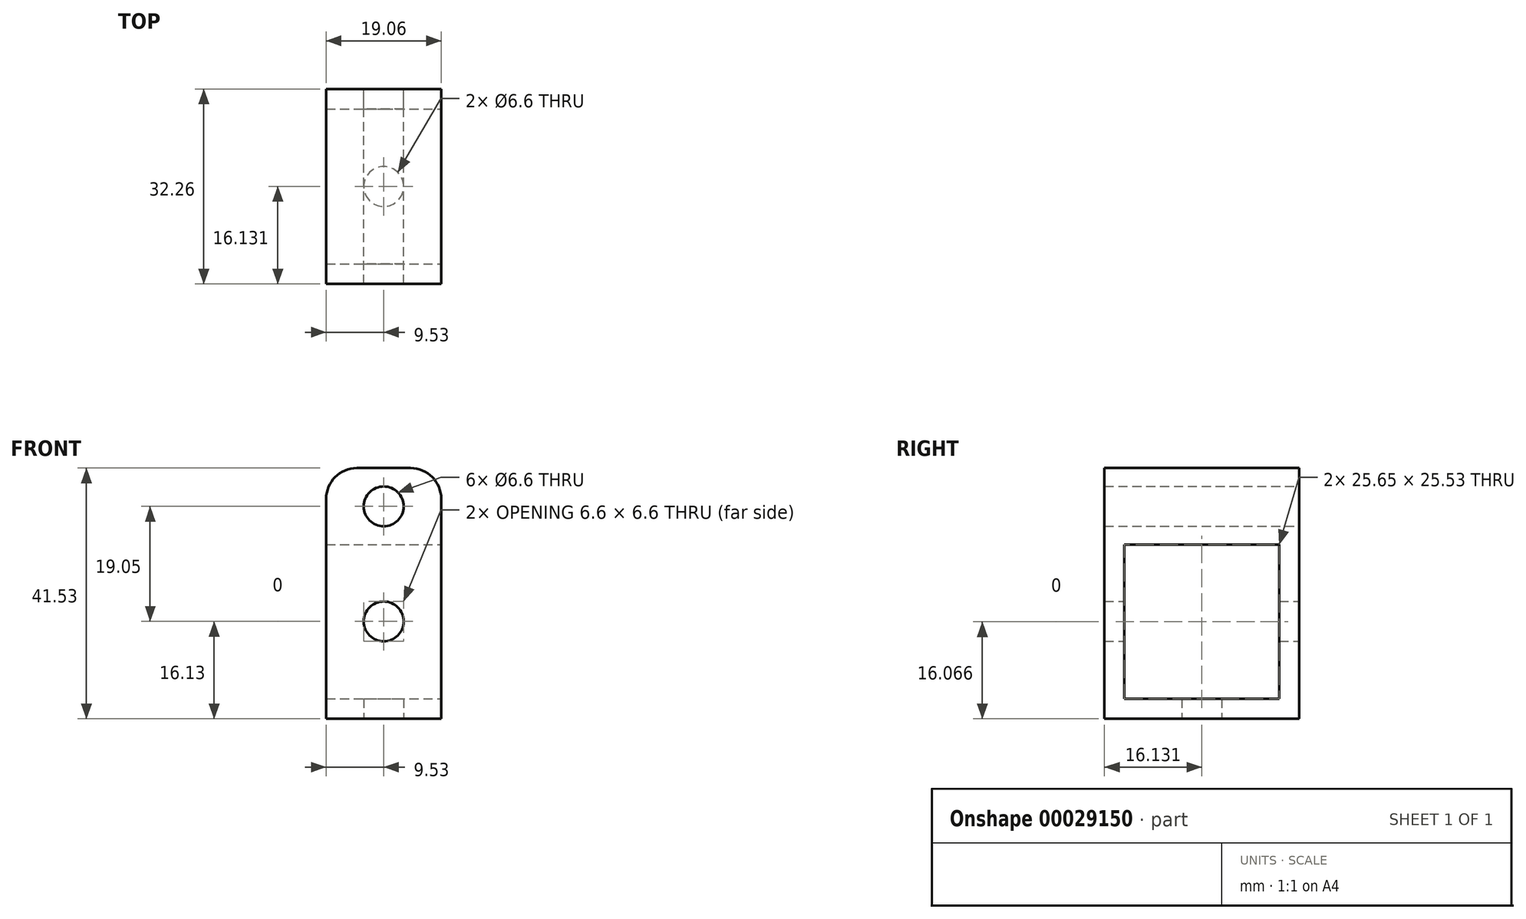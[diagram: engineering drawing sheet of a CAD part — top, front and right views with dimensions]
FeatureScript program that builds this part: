
annotation { "Feature Type Name" : "Feature", "Feature Type Description" : "" }
export const myFeature = defineFeature(function(context is Context, id is Id, definition is map)
    precondition{}
    {
        {
            var Q0;
            Q0=qCreatedBy(makeId("Front.planeOp"),FACE);
            var sketch = newSketch(context, id + "F0", { "sketchPlane" : qUnion([Q0])});
            skLineSegment(sketch, "E0", {"start": v(-9.53, 0) * mm, "end": v(0, 0) * mm, "construction": true});
            skLineSegment(sketch, "E1", {"start": v(-9.53, 0) * mm, "end": v(-9.53, 12.7) * mm});
            skLineSegment(sketch, "E2", {"start": v(-9.53, 12.7) * mm, "end": v(0, 12.7) * mm});
            skLineSegment(sketch, "E3", {"start": v(-9.53, 0) * mm, "end": v(-9.53, -28.83) * mm});
            skLineSegment(sketch, "E4", {"start": v(-9.53, -28.83) * mm, "end": v(0, -28.83) * mm});
            skLineSegment(sketch, "E5.MirrorCS", {"start": v(9.53, 12.7) * mm, "end": v(0, 12.7) * mm});
            skLineSegment(sketch, "E6.MirrorCS", {"start": v(9.53, 0) * mm, "end": v(9.53, 12.7) * mm});
            skLineSegment(sketch, "E7.MirrorCS", {"start": v(9.53, 0) * mm, "end": v(9.53, -28.83) * mm});
            skLineSegment(sketch, "E8.MirrorCS", {"start": v(9.53, -28.83) * mm, "end": v(0, -28.83) * mm});
            skLineSegment(sketch, "E9", {"start": v(0, 12.7) * mm, "end": v(0, 0) * mm, "construction": true});
            skCircle(sketch, "E10", {"center": v(0, 6.35) * mm, "radius": 3.3 * mm});
            skLineSegment(sketch, "E11", {"start": v(0, 0) * mm, "end": v(0, -25.4) * mm, "construction": true});
            skLineSegment(sketch, "E12", {"start": v(0, -25.4) * mm, "end": v(0, -28.83) * mm, "construction": true});
            skCircle(sketch, "E13", {"center": v(0, -12.7) * mm, "radius": 3.3 * mm});
            skSolve(sketch);
        }
        {
            var Q0;
            Q0=makeQuery(id+"F0.imprint","IMPRINT",FACE,{"disambiguationData":[TD([[makeQuery(id+"F0.imprint","IMPRINT",EDGE,{"derivedFrom":sQuery(id+"F0.wireOp",EDGE,"E1")}),-1.0]])]});
            extrude(context, id + "F1", {"entities" : qUnion([Q0]), "depth" : 32.26 * mm});
        }
        {
            var Q0;
            Q0=makeQuery(id+"F1.opExtrude","SWEPT_FACE",FACE,{"disambiguationData":[OSD([sQuery(id+"F0.wireOp",EDGE,"E6.MirrorCS"),sQuery(id+"F0.wireOp",EDGE,"E7.MirrorCS")])]});
            var sketch = newSketch(context, id + "F2", { "sketchPlane" : qUnion([Q0])});
            skLineSegment(sketch, "E14", {"start": v(-32.26, -25.53) * mm, "end": v(-28.96, -25.53) * mm, "construction": true});
            skLineSegment(sketch, "E15", {"start": v(-28.96, -25.53) * mm, "end": v(-3.3, -25.53) * mm, "construction": true});
            skLineSegment(sketch, "E16", {"start": v(-3.3, -25.53) * mm, "end": v(0, -25.53) * mm, "construction": true});
            skLineSegment(sketch, "E17", {"start": v(-16.13, -28.83) * mm, "end": v(-16.13, -25.53) * mm, "construction": true});
            skLineSegment(sketch, "E18", {"start": v(-28.96, -25.53) * mm, "end": v(-28.96, 0) * mm});
            skLineSegment(sketch, "E19", {"start": v(-28.96, -25.53) * mm, "end": v(-3.3, -25.53) * mm});
            skLineSegment(sketch, "E20", {"start": v(-3.3, -25.53) * mm, "end": v(-3.3, 0) * mm});
            skLineSegment(sketch, "E21", {"start": v(-3.3, 0) * mm, "end": v(-28.96, 0) * mm});
            skSolve(sketch);
        }
        {
            var Q0;
            Q0 = qSketchRegion(id + "F2", true);
            extrude(context, id + "F3", {"entities" : qUnion([Q0]), "operationType" : NewBodyOperationType.REMOVE, "oppositeDirection" : true, "depth" : 25.4 * mm});
        }
        {
            var Q0;
            Q0=makeQuery(id+"F1.opExtrude","SWEPT_FACE",FACE,{"disambiguationData":[OSD([sQuery(id+"F0.wireOp",EDGE,"E4"),sQuery(id+"F0.wireOp",EDGE,"E8.MirrorCS")])]});
            var sketch = newSketch(context, id + "F4", { "sketchPlane" : qUnion([Q0])});
            skLineSegment(sketch, "E22", {"start": v(0, 32.26) * mm, "end": v(0, 0) * mm, "construction": true});
            skCircle(sketch, "E23", {"center": v(0, 16.13) * mm, "radius": 3.3 * mm});
            skSolve(sketch);
        }
        {
            var Q0;
            Q0=makeQuery(id+"F4.imprint","IMPRINT",FACE,{"disambiguationData":[TD([[makeQuery(id+"F4.imprint","IMPRINT",EDGE,{"derivedFrom":sQuery(id+"F4.wireOp",EDGE,"E23")}),1.0]])]});
            extrude(context, id + "F5", {"entities" : qUnion([Q0]), "operationType" : NewBodyOperationType.REMOVE, "oppositeDirection" : true, "depth" : 12.7 * mm});
        }
        {
            var Q0;
            Q0=makeQuery(id+"F1.opExtrude","SWEPT_EDGE",EDGE,{"disambiguationData":[OSD([sQuery(id+"F0.wireOp",EDGE,"E5.MirrorCS"),sQuery(id+"F0.wireOp",EDGE,"E6.MirrorCS")])]});
            fillet(context, id + "F6", {"entities" : qUnion([Q0]), "radius" : 5.08 * mm, "tangentPropagation" : true, "allowEdgeOverflow" : false});
        }
        {
            var Q0;
            Q0=makeQuery(id+"F1.opExtrude","SWEPT_EDGE",EDGE,{"disambiguationData":[OSD([sQuery(id+"F0.wireOp",EDGE,"E1"),sQuery(id+"F0.wireOp",EDGE,"E2")])]});
            fillet(context, id + "F7", {"entities" : qUnion([Q0]), "radius" : 5.08 * mm, "tangentPropagation" : true, "allowEdgeOverflow" : false});
        }
    });
